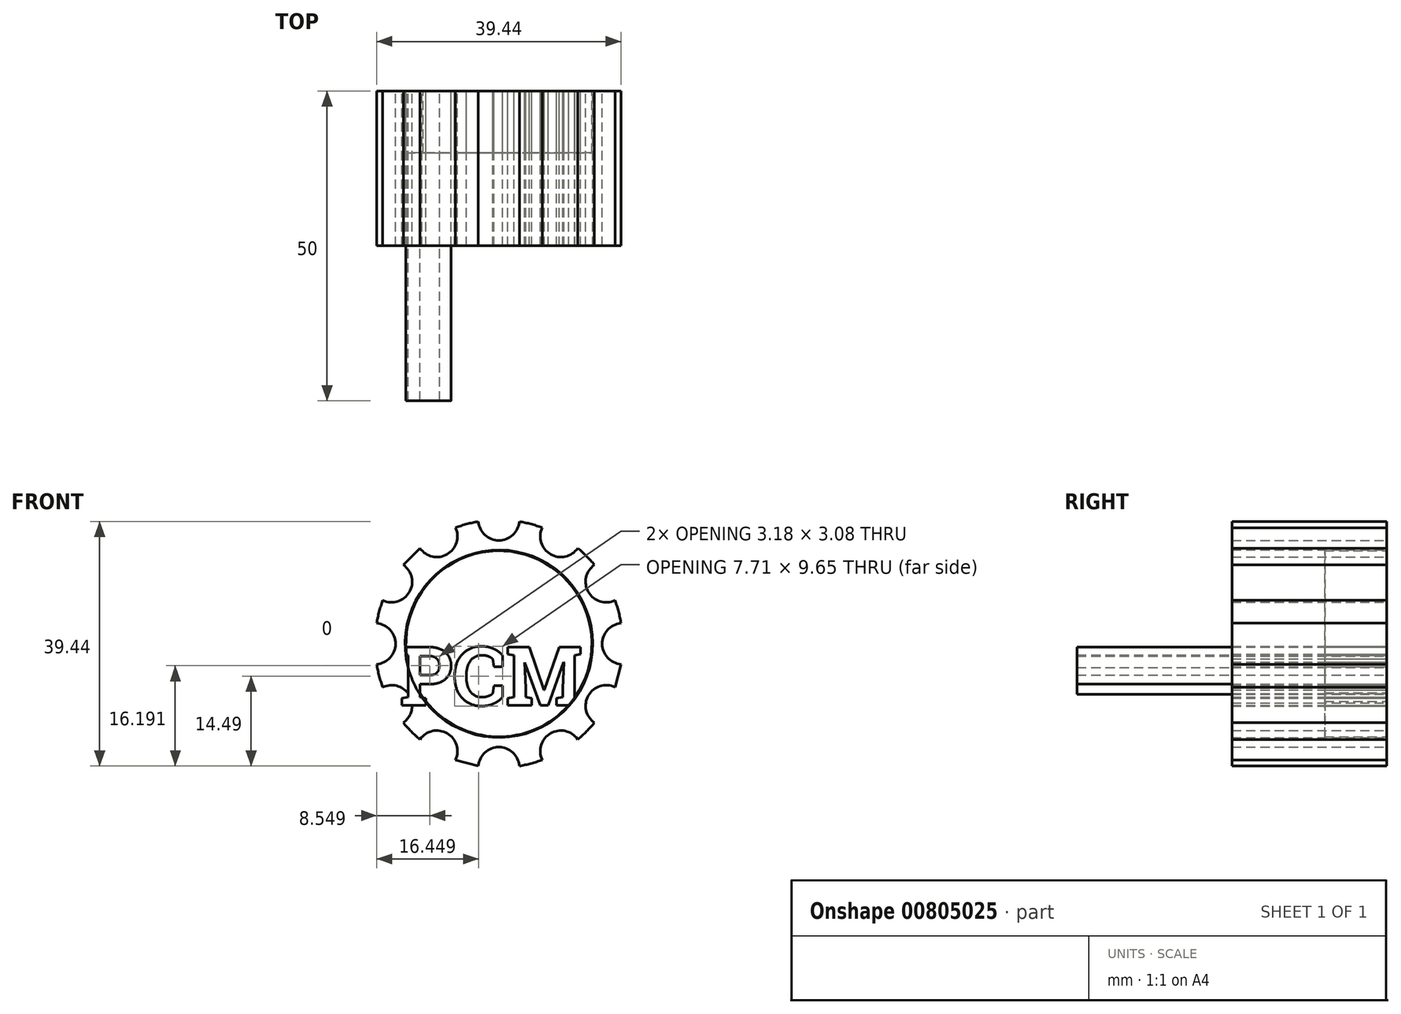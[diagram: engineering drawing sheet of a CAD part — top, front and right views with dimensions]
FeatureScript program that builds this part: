
annotation { "Feature Type Name" : "Feature", "Feature Type Description" : "" }
export const myFeature = defineFeature(function(context is Context, id is Id, definition is map)
    precondition{}
    {
        {
            var Q0;
            Q0=qCreatedBy(makeId("Front.planeOp"),FACE);
            var sketch = newSketch(context, id + "F0", { "sketchPlane" : qUnion([Q0])});
            skArc(sketch, "E0", {"start": v(-3.31, 19.72) * mm, "mid": v(-5.18, 19.32) * mm, "end": v(-7, 18.74) * mm});
            skCircle(sketch, "E1", {"center": v(0, 0) * mm, "radius": 15 * mm});
            skArc(sketch, "E2", {"start": v(-3.31, 19.72) * mm, "mid": v(0, 16.68) * mm, "end": v(3.31, 19.72) * mm});
            skArc(sketch, "E3.1.0", {"start": v(-12.73, 15.43) * mm, "mid": v(-8.34, 14.44) * mm, "end": v(-7, 18.74) * mm});
            skArc(sketch, "E3.2.0", {"start": v(-18.74, 7) * mm, "mid": v(-14.44, 8.34) * mm, "end": v(-15.43, 12.73) * mm});
            skArc(sketch, "E3.3.0", {"start": v(-19.72, -3.31) * mm, "mid": v(-16.68, 0) * mm, "end": v(-19.72, 3.31) * mm});
            skArc(sketch, "E3.4.0", {"start": v(-15.43, -12.73) * mm, "mid": v(-14.44, -8.34) * mm, "end": v(-18.74, -7) * mm});
            skArc(sketch, "E3.5.0", {"start": v(-7, -18.74) * mm, "mid": v(-8.34, -14.44) * mm, "end": v(-12.73, -15.43) * mm});
            skArc(sketch, "E3.6.0", {"start": v(3.31, -19.72) * mm, "mid": v(0, -16.68) * mm, "end": v(-3.31, -19.72) * mm});
            skArc(sketch, "E3.7.0", {"start": v(12.73, -15.43) * mm, "mid": v(8.34, -14.44) * mm, "end": v(7, -18.74) * mm});
            skArc(sketch, "E3.8.0", {"start": v(18.74, -7) * mm, "mid": v(14.44, -8.34) * mm, "end": v(15.43, -12.73) * mm});
            skArc(sketch, "E3.9.0", {"start": v(19.72, 3.31) * mm, "mid": v(16.68, 0) * mm, "end": v(19.72, -3.31) * mm});
            skArc(sketch, "E3.10.0", {"start": v(15.43, 12.73) * mm, "mid": v(14.44, 8.34) * mm, "end": v(18.74, 7) * mm});
            skArc(sketch, "E3.11.0", {"start": v(7, 18.74) * mm, "mid": v(8.34, 14.44) * mm, "end": v(12.73, 15.43) * mm});
            skArc(sketch, "E4.trimOffspring", {"start": v(-18.74, 7) * mm, "mid": v(-19.32, 5.18) * mm, "end": v(-19.72, 3.31) * mm});
            skArc(sketch, "E5.trimOffspring", {"start": v(-19.72, -3.31) * mm, "mid": v(-19.32, -5.18) * mm, "end": v(-18.74, -7) * mm});
            skArc(sketch, "E6.trimOffspring", {"start": v(-15.43, -12.73) * mm, "mid": v(-14.14, -14.14) * mm, "end": v(-12.73, -15.43) * mm});
            skArc(sketch, "E7.trimOffspring", {"start": v(3.31, -19.72) * mm, "mid": v(5.18, -19.32) * mm, "end": v(7, -18.74) * mm});
            skArc(sketch, "E8.trimOffspring", {"start": v(12.73, -15.43) * mm, "mid": v(14.14, -14.14) * mm, "end": v(15.43, -12.73) * mm});
            skArc(sketch, "E9.trimOffspring", {"start": v(19.72, 3.31) * mm, "mid": v(19.32, 5.18) * mm, "end": v(18.74, 7) * mm});
            skArc(sketch, "E10.trimOffspring", {"start": v(15.43, 12.73) * mm, "mid": v(14.14, 14.14) * mm, "end": v(12.73, 15.43) * mm});
            skArc(sketch, "E11.trimOffspring", {"start": v(7, 18.74) * mm, "mid": v(5.18, 19.32) * mm, "end": v(3.31, 19.72) * mm});
            skLineSegment(sketch, "E12", {"start": v(-12.73, 15.43) * mm, "end": v(-15.43, 12.73) * mm});
            skLineSegment(sketch, "E13", {"start": v(18.74, -7) * mm, "end": v(19.72, -3.31) * mm});
            skText(sketch, "E14", { "text": "PCM", "fontName": "RobotoSlab-Bold.ttf"});
            skLineSegment(sketch, "E15", {"start": v(-7, -18.74) * mm, "end": v(-3.31, -19.72) * mm});
            skCircle(sketch, "E16", {"center": v(0, 0) * mm, "radius": 15.13 * mm});
            const initialGuessF0  = {"E14": [-0.016, -0.00992, 1, 0, 0.0095]};
            skSetInitialGuess(sketch, initialGuessF0);
            skSolve(sketch);
        }
        {
            var Q0;
            Q0=makeQuery(id+"F0.imprint","IMPRINT",FACE,{"disambiguationData":[TD([[makeQuery(id+"F0.imprint","IMPRINT",EDGE,{"derivedFrom":sQuery(id+"F0.wireOp",EDGE,"E0")}),1.0]])]});
            var Q1;
            Q1=makeQuery(id+"F0.imprint","IMPRINT",FACE,{"disambiguationData":[TD([[makeQuery(id+"F0.imprint","IMPRINT",EDGE,{"derivedFrom":sQuery(id+"F0.wireOp",EDGE,"E14.sketch_text.stroke-0")}),-1.0]])]});
            var Q2;
            Q2=makeQuery(id+"F0.imprint","IMPRINT",FACE,{"disambiguationData":[TD([[makeQuery(id+"F0.imprint","IMPRINT",EDGE,{"derivedFrom":sQuery(id+"F0.wireOp",EDGE,"E14.sketch_text.stroke-23")}),-1.0]])]});
            var Q3;
            Q3=makeQuery(id+"F0.imprint","IMPRINT",FACE,{"disambiguationData":[TD([[makeQuery(id+"F0.imprint","IMPRINT",EDGE,{"derivedFrom":sQuery(id+"F0.wireOp",EDGE,"E14.sketch_text.stroke-47")}),-1.0]])]});
            var Q4;
            {var subQ3=sQuery(id+"F0.wireOp",EDGE,"E1");var subQ8=sQuery(id+"F0.wireOp",EDGE,"E14.sketch_text.stroke-11");var subQ10=makeQuery(id+"F0.imprint","INTERSECT",VERTEX,{"derivedFrom":[subQ3,subQ8]});Q4=makeQuery(id+"F0.imprint","IMPRINT",FACE,{"disambiguationData":[TD([[makeQuery(id+"F0.imprint","IMPRINT",EDGE,{"disambiguationData":[TD([[subQ10,-1.0]])],"derivedFrom":subQ3}),-1.0]])]});}
            var Q5;
            {var subQ5=sQuery(id+"F0.wireOp",EDGE,"E14.sketch_text.stroke-13");Q5=makeQuery(id+"F0.imprint","IMPRINT",FACE,{"disambiguationData":[TD([[makeQuery(id+"F0.imprint","IMPRINT",EDGE,{"derivedFrom":subQ5}),-1.0]])]});}
            var Q6;
            {var subQ5=sQuery(id+"F0.wireOp",EDGE,"E14.sketch_text.stroke-72");Q6=makeQuery(id+"F0.imprint","IMPRINT",FACE,{"disambiguationData":[TD([[makeQuery(id+"F0.imprint","IMPRINT",EDGE,{"derivedFrom":subQ5}),-1.0]])]});}
            extrude(context, id + "F1", {"entities" : qUnion([Q0, Q1, Q2, Q3, Q4, Q5, Q6]), "depth" : 25 * mm, "offsetDistance" : 25 * mm});
        }
        {
            var Q0;
            Q0=makeQuery(id+"F0.imprint","IMPRINT",FACE,{"disambiguationData":[TD([[makeQuery(id+"F0.imprint","IMPRINT",EDGE,{"derivedFrom":sQuery(id+"F0.wireOp",EDGE,"E14.sketch_text.stroke-0")}),1.0]])]});
            extrude(context, id + "F2", {"entities" : qUnion([Q0]), "depth" : 10 * mm, "offsetDistance" : 25 * mm});
        }
        {
            var Q0;
            Q0=makeQuery(id+"F1.opExtrude","CAP_FACE",FACE,{"disambiguationData":[OSD([sQuery(id+"F0.wireOp",EDGE,"E1"),sQuery(id+"F0.wireOp",EDGE,"E14.sketch_text.stroke-0"),sQuery(id+"F0.wireOp",EDGE,"E14.sketch_text.stroke-1"),sQuery(id+"F0.wireOp",EDGE,"E14.sketch_text.stroke-2"),sQuery(id+"F0.wireOp",EDGE,"E14.sketch_text.stroke-3"),sQuery(id+"F0.wireOp",EDGE,"E14.sketch_text.stroke-4"),sQuery(id+"F0.wireOp",EDGE,"E14.sketch_text.stroke-5"),sQuery(id+"F0.wireOp",EDGE,"E14.sketch_text.stroke-11"),sQuery(id+"F0.wireOp",EDGE,"E14.sketch_text.stroke-12"),sQuery(id+"F0.wireOp",EDGE,"E14.sketch_text.stroke-14"),sQuery(id+"F0.wireOp",EDGE,"E14.sketch_text.stroke-15"),sQuery(id+"F0.wireOp",EDGE,"E14.sketch_text.stroke-16"),sQuery(id+"F0.wireOp",EDGE,"E14.sketch_text.stroke-17"),sQuery(id+"F0.wireOp",EDGE,"E14.sketch_text.stroke-18"),sQuery(id+"F0.wireOp",EDGE,"E14.sketch_text.stroke-19"),sQuery(id+"F0.wireOp",EDGE,"E14.sketch_text.stroke-20"),sQuery(id+"F0.wireOp",EDGE,"E14.sketch_text.stroke-21"),sQuery(id+"F0.wireOp",EDGE,"E14.sketch_text.stroke-22"),sQuery(id+"F0.wireOp",EDGE,"E16")])],"isStart":false});
            var Q1;
            {var subQ0=sQuery(id+"F0.wireOp",EDGE,"E14.sketch_text.stroke-8");var subQ10=sQuery(id+"F0.wireOp",EDGE,"E3.4.0");var subQ14=makeQuery(id+"F0.imprint","INTERSECT",VERTEX,{"derivedFrom":[subQ10,subQ0]});Q1=makeQuery(id+"F0.imprint","IMPRINT",FACE,{"disambiguationData":[TD([[makeQuery(id+"F0.imprint","IMPRINT",EDGE,{"disambiguationData":[TD([[subQ14,-1.0]])],"derivedFrom":subQ10}),-1.0]])]});}
            var Q2;
            {var subQ1=sQuery(id+"F0.wireOp",EDGE,"E14.sketch_text.stroke-9");Q2=makeQuery(id+"F0.imprint","IMPRINT",FACE,{"disambiguationData":[TD([[makeQuery(id+"F0.imprint","IMPRINT",EDGE,{"derivedFrom":subQ1}),-1.0]])]});}
            extrude(context, id + "F3", {"entities" : qUnion([Q0, Q1, Q2]), "depth" : 25 * mm, "offsetDistance" : 25 * mm});
        }
    });
